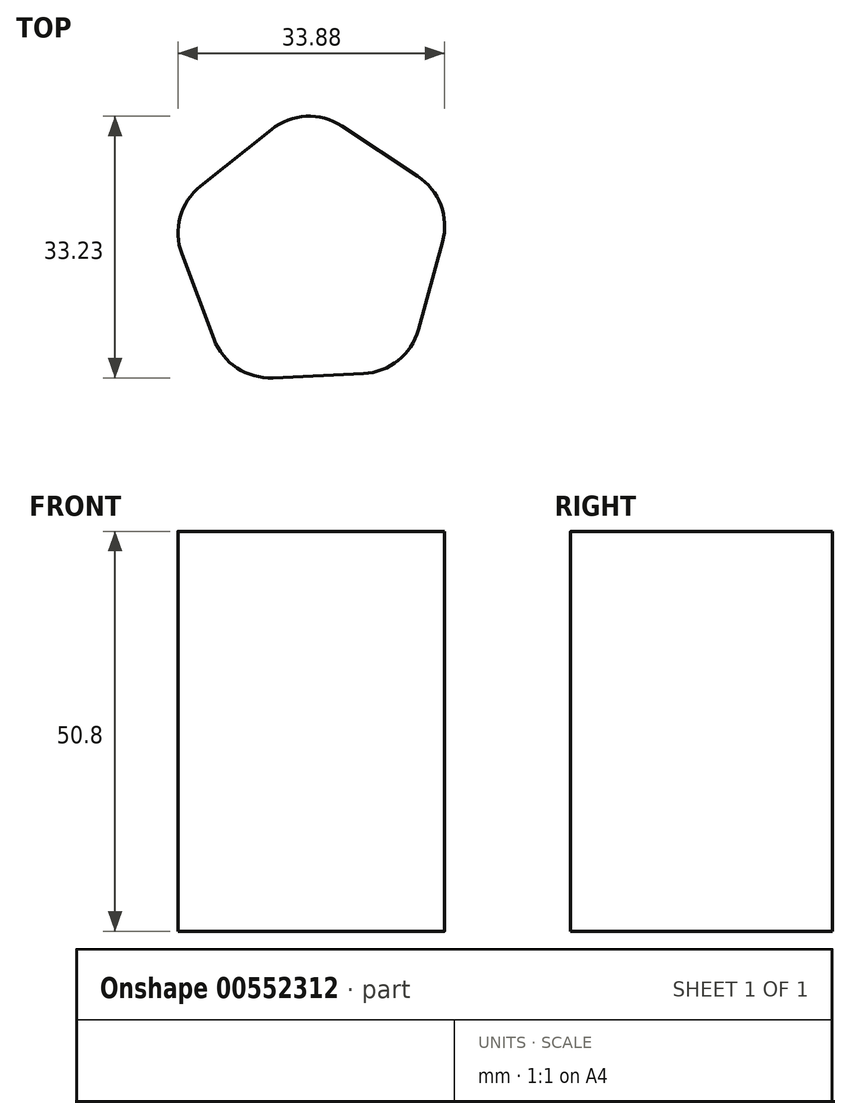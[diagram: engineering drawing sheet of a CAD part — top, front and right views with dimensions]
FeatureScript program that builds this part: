
annotation { "Feature Type Name" : "Feature", "Feature Type Description" : "" }
export const myFeature = defineFeature(function(context is Context, id is Id, definition is map)
    precondition{}
    {
        {
            var Q0;
            Q0=qCreatedBy(makeId("Top.planeOp"),FACE);
            var sketch = newSketch(context, id + "F0", { "sketchPlane" : qUnion([Q0])});
            skCircle(sketch, "E0.cCircle", {"center": v(-40.94, 44.64) * mm, "radius": 19.23 * mm, "construction": true});
            skLineSegment(sketch, "E0.0", {"start": v(-34.46, 29.37) * mm, "end": v(-45.98, 28.84) * mm});
            skLineSegment(sketch, "E0.1", {"start": v(-53.46, 33.76) * mm, "end": v(-57.53, 44.55) * mm});
            skLineSegment(sketch, "E0.2", {"start": v(-55.16, 53.19) * mm, "end": v(-46.15, 60.39) * mm});
            skLineSegment(sketch, "E0.3", {"start": v(-37.2, 60.8) * mm, "end": v(-27.57, 54.47) * mm});
            skLineSegment(sketch, "E0.4", {"start": v(-24.41, 46.09) * mm, "end": v(-27.46, 34.97) * mm});
            skPoint(sketch, "E1.visualSharp", {"position": v(-41.83, 63.85) * mm});
            skArc(sketch, "E1.filletArc", {"start": v(-37.2, 60.8) * mm, "mid": v(-41.75, 62.05) * mm, "end": v(-46.15, 60.39) * mm});
            skPoint(sketch, "E2.visualSharp", {"position": v(-59.48, 49.73) * mm});
            skArc(sketch, "E2.filletArc", {"start": v(-55.16, 53.19) * mm, "mid": v(-57.74, 49.25) * mm, "end": v(-57.53, 44.55) * mm});
            skPoint(sketch, "E3.visualSharp", {"position": v(-51.5, 28.58) * mm});
            skArc(sketch, "E3.filletArc", {"start": v(-53.46, 33.76) * mm, "mid": v(-50.52, 30.08) * mm, "end": v(-45.98, 28.84) * mm});
            skPoint(sketch, "E4.visualSharp", {"position": v(-28.93, 29.63) * mm});
            skArc(sketch, "E4.filletArc", {"start": v(-34.46, 29.37) * mm, "mid": v(-30.05, 31.03) * mm, "end": v(-27.46, 34.97) * mm});
            skPoint(sketch, "E5.visualSharp", {"position": v(-22.95, 51.42) * mm});
            skArc(sketch, "E5.filletArc", {"start": v(-24.41, 46.09) * mm, "mid": v(-24.63, 50.79) * mm, "end": v(-27.57, 54.47) * mm});
            skSolve(sketch);
        }
        {
            var Q0;
            Q0=makeQuery(id+"F0.imprint","IMPRINT",FACE,{"disambiguationData":[TD([[makeQuery(id+"F0.imprint","IMPRINT",EDGE,{"derivedFrom":sQuery(id+"F0.wireOp",EDGE,"E0.0")}),-1.0]])]});
            extrude(context, id + "F1", {"entities" : qUnion([Q0]), "depth" : 50.8 * mm, "offsetDistance" : 25.4 * mm});
        }
    });
